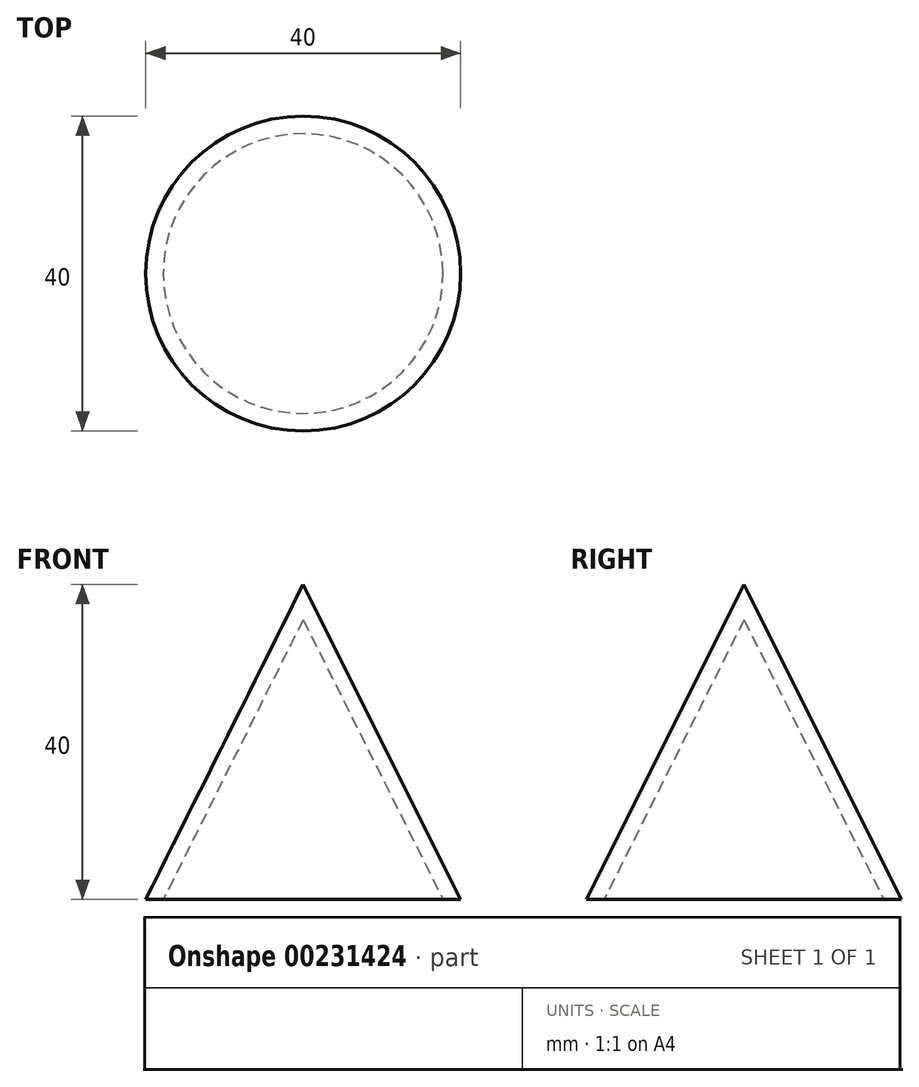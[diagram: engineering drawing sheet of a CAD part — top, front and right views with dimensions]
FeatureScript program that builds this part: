
annotation { "Feature Type Name" : "Feature", "Feature Type Description" : "" }
export const myFeature = defineFeature(function(context is Context, id is Id, definition is map)
    precondition{}
    {
        {
            var Q0;
            Q0=qCreatedBy(makeId("Front.planeOp"),FACE);
            var sketch = newSketch(context, id + "F0", { "sketchPlane" : qUnion([Q0])});
            skLineSegment(sketch, "E0.bottom", {"start": v(0, 0) * mm, "end": v(20, 0) * mm});
            skLineSegment(sketch, "E0.left", {"start": v(0, 0) * mm, "end": v(0, 40) * mm});
            skLineSegment(sketch, "E1", {"start": v(20, 0) * mm, "end": v(0, 40) * mm});
            skSolve(sketch);
        }
        {
            var Q0;
            Q0=makeQuery(id+"F0.imprint","IMPRINT",FACE,{"disambiguationData":[TD([[makeQuery(id+"F0.imprint","IMPRINT",EDGE,{"derivedFrom":sQuery(id+"F0.wireOp",EDGE,"E0.bottom")}),1.0]])]});
            var Q1;
            Q1=sQuery(id+"F0.wireOp",EDGE,"E0.left");
            revolve(context, id + "F1", {"entities" : qUnion([Q0]), "axis" : qUnion([Q1]), "revolveType" : RevolveType.FULL});
        }
        {
            var Q0;
            Q0=qCreatedBy(makeId("Top.planeOp"),FACE);
            cPlane(context, id + "F2", {"entities" : qUnion([Q0]), "cplaneType" : CPlaneType.OFFSET, "offset" : 20 * mm, "width" : 150 * mm, "height" : 150 * mm});
        }
        {
            var Q0;
            Q0=makeQuery(id+"F1.opRevolve","SWEPT_FACE",FACE,{"disambiguationData":[OSD([sQuery(id+"F0.wireOp",EDGE,"E0.bottom")])]});
            shell(context, id + "F3", {"entities" : qUnion([Q0]), "thickness" : 2 * mm});
        }
    });
